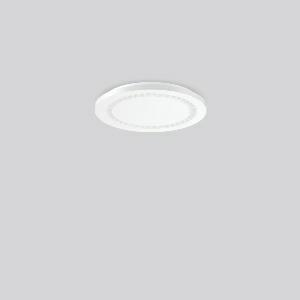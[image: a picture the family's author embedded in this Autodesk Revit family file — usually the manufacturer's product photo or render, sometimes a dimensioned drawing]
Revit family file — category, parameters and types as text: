
# Revit family: hemis_round_312185_002_3_8aee
name_source: partatom
category: Lighting Fixtures
units: mm (PartAtom-declared; Revit-internal decimal feet)

## family parameters
Cut with Voids When Loaded = No
Host = Face
Light Source = No
Part Type = Normal
Room Calculation Point = No
Round Connector Dimension = Use Diameter
Shared = No

## types (1)
- MultiLumen 1 (1 x LED Modul 840, 1950 lm, 4000)
    Apparent Load = 16 VA
    CIE Flux Codes = 87 99 100 100 100
    Color Rendering = 80
    Color Temperature = 4000
    Default Elevation = 1800 mm
    Description = Series: HEMIS round
Glare-free LED ceiling luminaire with optical lens system. Base: metal, powder-coated, with bayonet fixing. Housing: plastic (polycarbonate). Housing and diffuser are screwed together. Diffuser with optic lenses. Big terminal block; ideal for through-wiring. Sealing strip on the back of the luminaire connects seamlessly with the ceiling. Easy installation with Plug+Play plug connection. Thanks to RUG < 22 ideal for corridors, stairways, shops, schools, meeting rooms, rest areas. 
Colour: white
Diameter: 300 mm
Height: 33 mm
Lamp: LED
Socket: without socket
Colour temperature: 4000K
Colour rendering index (CRI): 80
System power: 16 W
Rated luminous flux: 1950 lm
Luminous efficiency: 122 lm/W
System power 2: 10 W
Rated luminous flux 2: 1250 lm
Luminous efficiency 2: 125 lm/W
Control gear: Regulated power supply
Protection class: I
Type of protection: IP 40
    Height = 33 mm
    Lamp = 1 x LED Modul 840
    Lamp Light Flux = 1950 lm
    Lamp count = 1
    Length = 300 mm
    Lifetime = 50000 h
    Luminous efficacy = 122 lm/W
    Manufacturer = RZB
    ModVariant = No
    Model = 312185.002.3
    Mounting Place = Ceiling
    Mounting Type = Surface mounted
    Number of Poles = 1
    OnlyDefault = Yes
    Power Factor = 1
    Product Name = HEMIS round
    Product group = Surface mounted modular luminaires
    ProductGroupID = 306
    Protection Class = Protection class I
    Protection Degree = Degree of protection
    RLX_Detail_Level = 1
    RLX_Emergency_Light_Flux = 0 lm
    RLX_Emergency_Type = 0
    RLX_Emergency_Type_DB = No
    RlxData = <blob elided: 40513 chars, md5=e6e5e94b>
    Socket = socket
    Standby Power = 0 W
    System Light Flux = 1950 lm
    System Power = 16 W
    Type Comments = MultiLumen 1
    Type Image = 312185.002.jpg
    URL = http://relux.com
    VarID = multilumen_1
    Voltage = 0 V
    Weight = 0.00 kg
    Width = 0 mm  [stored 0 ft]

note: [stored X ft] marks values corroborated as IEEE doubles in the binary element streams (Revit-internal decimal feet)

## geometry (parser evidence)
native form markers: Blend x4, Sweep x9
no freeform markers — native parametric forms only
